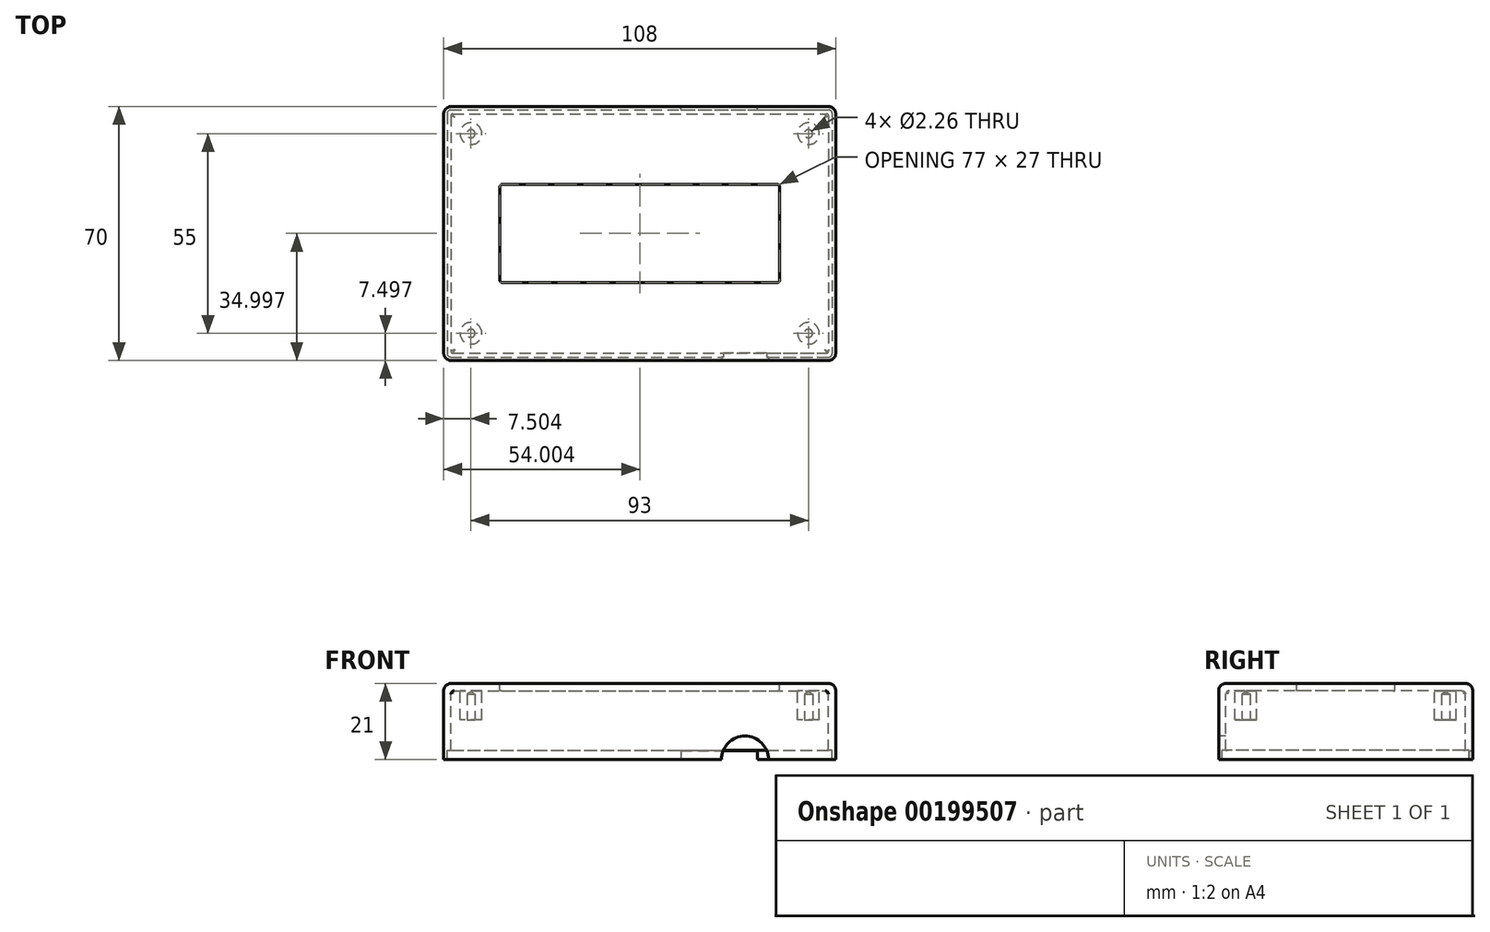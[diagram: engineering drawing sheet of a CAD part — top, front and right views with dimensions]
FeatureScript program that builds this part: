
annotation { "Feature Type Name" : "Feature", "Feature Type Description" : "" }
export const myFeature = defineFeature(function(context is Context, id is Id, definition is map)
    precondition{}
    {
        {
            var Q0;
            Q0=qCreatedBy(makeId("Top.planeOp"),FACE);
            var sketch = newSketch(context, id + "F0", { "sketchPlane" : qUnion([Q0])});
            skLineSegment(sketch, "E0.bottom", {"start": v(-55.54, 34.04) * mm, "end": v(48.46, 34.04) * mm});
            skLineSegment(sketch, "E0.top", {"start": v(-55.54, -35.96) * mm, "end": v(48.46, -35.96) * mm});
            skLineSegment(sketch, "E0.left", {"start": v(-57.54, 32.04) * mm, "end": v(-57.54, -33.96) * mm});
            skLineSegment(sketch, "E0.right", {"start": v(50.46, 32.04) * mm, "end": v(50.46, -33.96) * mm});
            skLineSegment(sketch, "E1.bottom", {"start": v(-41.54, 12.54) * mm, "end": v(34.46, 12.54) * mm});
            skLineSegment(sketch, "E1.top", {"start": v(-41.54, -14.46) * mm, "end": v(34.46, -14.46) * mm});
            skLineSegment(sketch, "E1.left", {"start": v(-42.04, 12.04) * mm, "end": v(-42.04, -13.96) * mm});
            skLineSegment(sketch, "E1.right", {"start": v(34.96, 12.04) * mm, "end": v(34.96, -13.96) * mm});
            skLineSegment(sketch, "E2.bottom", {"start": v(-55.04, 32.04) * mm, "end": v(47.96, 32.04) * mm});
            skLineSegment(sketch, "E2.top", {"start": v(-55.04, -33.96) * mm, "end": v(47.96, -33.96) * mm});
            skLineSegment(sketch, "E2.left", {"start": v(-55.54, 31.54) * mm, "end": v(-55.54, -33.46) * mm});
            skLineSegment(sketch, "E2.right", {"start": v(48.46, 31.54) * mm, "end": v(48.46, -33.46) * mm});
            skCircle(sketch, "E3", {"center": v(-50.04, 26.54) * mm, "radius": 3 * mm});
            skCircle(sketch, "E4", {"center": v(42.96, 26.54) * mm, "radius": 3 * mm});
            skCircle(sketch, "E5", {"center": v(-50.04, -28.46) * mm, "radius": 3 * mm});
            skCircle(sketch, "E6", {"center": v(42.96, -28.46) * mm, "radius": 3 * mm});
            skPoint(sketch, "E7.visualSharp", {"position": v(-55.54, -33.96) * mm});
            skPoint(sketch, "E8.visualSharp", {"position": v(-55.54, 32.04) * mm});
            skPoint(sketch, "E9.visualSharp", {"position": v(48.46, 32.04) * mm});
            skPoint(sketch, "E10.visualSharp", {"position": v(48.46, -33.96) * mm});
            skPoint(sketch, "E11.visualSharp", {"position": v(-57.54, 34.04) * mm});
            skPoint(sketch, "E12.visualSharp", {"position": v(50.46, 34.04) * mm});
            skPoint(sketch, "E13.visualSharp", {"position": v(50.46, -35.96) * mm});
            skLineSegment(sketch, "E14.bottom", {"start": v(-55.64, 33.09) * mm, "end": v(48.56, 33.09) * mm});
            skLineSegment(sketch, "E14.top", {"start": v(-55.64, -35.01) * mm, "end": v(48.56, -35.01) * mm});
            skLineSegment(sketch, "E14.left", {"start": v(-56.59, 32.14) * mm, "end": v(-56.59, -34.06) * mm});
            skLineSegment(sketch, "E14.right", {"start": v(49.51, 32.14) * mm, "end": v(49.51, -34.06) * mm});
            skPoint(sketch, "E15.visualSharp", {"position": v(-42.04, 12.54) * mm});
            skArc(sketch, "E15.filletArc", {"start": v(-41.54, 12.54) * mm, "mid": v(-41.89, 12.4) * mm, "end": v(-42.04, 12.04) * mm});
            skPoint(sketch, "E16.visualSharp", {"position": v(34.96, 12.54) * mm});
            skArc(sketch, "E16.filletArc", {"start": v(34.96, 12.04) * mm, "mid": v(34.82, 12.4) * mm, "end": v(34.46, 12.54) * mm});
            skPoint(sketch, "E17.visualSharp", {"position": v(34.96, -14.46) * mm});
            skArc(sketch, "E17.filletArc", {"start": v(34.46, -14.46) * mm, "mid": v(34.82, -14.32) * mm, "end": v(34.96, -13.96) * mm});
            skPoint(sketch, "E18.visualSharp", {"position": v(-42.04, -14.46) * mm});
            skArc(sketch, "E18.filletArc", {"start": v(-42.04, -13.96) * mm, "mid": v(-41.89, -14.32) * mm, "end": v(-41.54, -14.46) * mm});
            skArc(sketch, "E19.filletArc", {"start": v(-55.04, 32.04) * mm, "mid": v(-55.39, 31.9) * mm, "end": v(-55.54, 31.54) * mm});
            skArc(sketch, "E20.filletArc", {"start": v(48.46, 31.54) * mm, "mid": v(48.32, 31.9) * mm, "end": v(47.96, 32.04) * mm});
            skArc(sketch, "E21.filletArc", {"start": v(47.96, -33.96) * mm, "mid": v(48.32, -33.82) * mm, "end": v(48.46, -33.46) * mm});
            skArc(sketch, "E22.filletArc", {"start": v(-55.54, -33.46) * mm, "mid": v(-55.39, -33.82) * mm, "end": v(-55.04, -33.96) * mm});
            skPoint(sketch, "E23.visualSharp", {"position": v(-56.59, 33.09) * mm});
            skArc(sketch, "E23.filletArc", {"start": v(-55.64, 33.09) * mm, "mid": v(-56.3, 32.8) * mm, "end": v(-56.59, 32.14) * mm});
            skPoint(sketch, "E24.visualSharp", {"position": v(-56.59, -35.01) * mm});
            skArc(sketch, "E24.filletArc", {"start": v(-56.59, -34.06) * mm, "mid": v(-56.3, -34.73) * mm, "end": v(-55.64, -35.01) * mm});
            skPoint(sketch, "E25.visualSharp", {"position": v(49.51, -35.01) * mm});
            skArc(sketch, "E25.filletArc", {"start": v(48.56, -35.01) * mm, "mid": v(49.24, -34.73) * mm, "end": v(49.51, -34.06) * mm});
            skPoint(sketch, "E26.visualSharp", {"position": v(49.51, 33.09) * mm});
            skArc(sketch, "E26.filletArc", {"start": v(49.51, 32.14) * mm, "mid": v(49.24, 32.8) * mm, "end": v(48.56, 33.09) * mm});
            skArc(sketch, "E27.filletArc", {"start": v(50.46, 32.04) * mm, "mid": v(49.88, 33.45) * mm, "end": v(48.46, 34.04) * mm});
            skArc(sketch, "E28.filletArc", {"start": v(48.46, -35.96) * mm, "mid": v(49.88, -35.38) * mm, "end": v(50.46, -33.96) * mm});
            skPoint(sketch, "E29.visualSharp", {"position": v(-57.54, -35.96) * mm});
            skArc(sketch, "E29.filletArc", {"start": v(-57.54, -33.96) * mm, "mid": v(-56.95, -35.38) * mm, "end": v(-55.54, -35.96) * mm});
            skArc(sketch, "E30.filletArc", {"start": v(-55.54, 34.04) * mm, "mid": v(-56.95, 33.45) * mm, "end": v(-57.54, 32.04) * mm});
            skSolve(sketch);
        }
        {
            var Q0;
            Q0=makeQuery(id+"F0.imprint","IMPRINT",FACE,{"disambiguationData":[TD([[makeQuery(id+"F0.imprint","IMPRINT",EDGE,{"derivedFrom":sQuery(id+"F0.wireOp",EDGE,"E2.bottom")}),1.0]])]});
            var Q1;
            Q1=makeQuery(id+"F0.imprint","IMPRINT",FACE,{"disambiguationData":[TD([[makeQuery(id+"F0.imprint","IMPRINT",EDGE,{"derivedFrom":sQuery(id+"F0.wireOp",EDGE,"E2.bottom")}),-1.0]])]});
            var Q2;
            Q2=makeQuery(id+"F0.imprint","IMPRINT",FACE,{"disambiguationData":[TD([[makeQuery(id+"F0.imprint","IMPRINT",EDGE,{"derivedFrom":sQuery(id+"F0.wireOp",EDGE,"E3")}),1.0]])]});
            var Q3;
            Q3=makeQuery(id+"F0.imprint","IMPRINT",FACE,{"disambiguationData":[TD([[makeQuery(id+"F0.imprint","IMPRINT",EDGE,{"derivedFrom":sQuery(id+"F0.wireOp",EDGE,"E4")}),1.0]])]});
            var Q4;
            Q4=makeQuery(id+"F0.imprint","IMPRINT",FACE,{"disambiguationData":[TD([[makeQuery(id+"F0.imprint","IMPRINT",EDGE,{"derivedFrom":sQuery(id+"F0.wireOp",EDGE,"E6")}),1.0]])]});
            var Q5;
            Q5=makeQuery(id+"F0.imprint","IMPRINT",FACE,{"disambiguationData":[TD([[makeQuery(id+"F0.imprint","IMPRINT",EDGE,{"derivedFrom":sQuery(id+"F0.wireOp",EDGE,"E5")}),1.0]])]});
            var Q6;
            Q6=makeQuery(id+"F0.imprint","IMPRINT",FACE,{"disambiguationData":[TD([[makeQuery(id+"F0.imprint","IMPRINT",EDGE,{"derivedFrom":sQuery(id+"F0.wireOp",EDGE,"E0.bottom")}),-1.0]])]});
            extrude(context, id + "F1", {"entities" : qUnion([Q0, Q1, Q2, Q3, Q4, Q5, Q6]), "oppositeDirection" : true, "depth" : 2 * mm});
        }
        {
            var Q0;
            Q0=makeQuery(id+"F0.imprint","IMPRINT",FACE,{"disambiguationData":[TD([[makeQuery(id+"F0.imprint","IMPRINT",EDGE,{"derivedFrom":sQuery(id+"F0.wireOp",EDGE,"E2.bottom")}),1.0]])]});
            extrude(context, id + "F2", {"entities" : qUnion([Q0]), "operationType" : NewBodyOperationType.ADD, "oppositeDirection" : true, "depth" : 18.49 * mm});
        }
        {
            var Q0;
            {var subQ0=sQuery(id+"F0.wireOp",EDGE,"E0.right");var subQ1=sQuery(id+"F0.wireOp",EDGE,"E0.left");var subQ2=sQuery(id+"F0.wireOp",EDGE,"E0.top");var subQ3=sQuery(id+"F0.wireOp",EDGE,"E0.bottom");Q0=makeQuery(id+"F2.boolean.opBoolean","SPLIT",FACE,{"disambiguationData":[TD([makeQuery(id+"F1.opExtrude","SWEPT_FACE",FACE,{"disambiguationData":[OSD([subQ3])]})])],"derivedFrom":makeQuery(id+"F1.opExtrude","CAP_FACE",FACE,{"disambiguationData":[OSD([subQ3,subQ2,subQ1,subQ0,sQuery(id+"F0.wireOp",EDGE,"E1.bottom"),sQuery(id+"F0.wireOp",EDGE,"E1.top"),sQuery(id+"F0.wireOp",EDGE,"E1.left"),sQuery(id+"F0.wireOp",EDGE,"E1.right"),sQuery(id+"F0.wireOp",EDGE,"TIqVLyNP-uRYi-IZCg-FFMY-wpAB1gUjtPzc"),sQuery(id+"F0.wireOp",EDGE,"eGpXYtko-bpSR-Pbzy-FSSL-hkfkqHyOyQKH"),sQuery(id+"F0.wireOp",EDGE,"aKAKSCUs-jV2O-gDTW-lYoO-wS98vJuitCCh"),sQuery(id+"F0.wireOp",EDGE,"Y9MBlFMN-f0e3-QmNQ-qzjT-em0skZvg3ODU")])],"isStart":false})});}
            extrude(context, id + "F3", {"entities" : qUnion([Q0]), "operationType" : NewBodyOperationType.ADD, "depth" : 19 * mm});
        }
        {
            var Q0;
            Q0=makeQuery(id+"F0.imprint","IMPRINT",FACE,{"disambiguationData":[TD([[makeQuery(id+"F0.imprint","IMPRINT",EDGE,{"derivedFrom":sQuery(id+"F0.wireOp",EDGE,"E3")}),1.0]])]});
            var Q1;
            Q1=makeQuery(id+"F0.imprint","IMPRINT",FACE,{"disambiguationData":[TD([[makeQuery(id+"F0.imprint","IMPRINT",EDGE,{"derivedFrom":sQuery(id+"F0.wireOp",EDGE,"E4")}),1.0]])]});
            var Q2;
            Q2=makeQuery(id+"F0.imprint","IMPRINT",FACE,{"disambiguationData":[TD([[makeQuery(id+"F0.imprint","IMPRINT",EDGE,{"derivedFrom":sQuery(id+"F0.wireOp",EDGE,"E5")}),1.0]])]});
            var Q3;
            Q3=makeQuery(id+"F0.imprint","IMPRINT",FACE,{"disambiguationData":[TD([[makeQuery(id+"F0.imprint","IMPRINT",EDGE,{"derivedFrom":sQuery(id+"F0.wireOp",EDGE,"E6")}),1.0]])]});
            extrude(context, id + "F4", {"entities" : qUnion([Q0, Q1, Q2, Q3]), "operationType" : NewBodyOperationType.ADD, "oppositeDirection" : true, "depth" : 10 * mm});
        }
        {
            var Q0;
            {var subQ0=sQuery(id+"F0.wireOp",EDGE,"E0.top");Q0=makeQuery(id+"F3.boolean.opBoolean","MERGE",FACE,{"derivedFrom":[makeQuery(id+"F1.opExtrude","SWEPT_FACE",FACE,{"disambiguationData":[OSD([subQ0])]}),makeQuery(id+"F3.opExtrude","SWEPT_FACE",FACE,{"disambiguationData":[OSD([subQ0])]})]});}
            var sketch = newSketch(context, id + "F5", { "sketchPlane" : qUnion([Q0])});
            skPoint(sketch, "E31", {"position": v(25.46, -21) * mm});
            skCircle(sketch, "E32", {"center": v(25.46, -21) * mm, "radius": 6.5 * mm});
            skSolve(sketch);
        }
        {
            var Q0;
            {var subQ0=sQuery(id+"F5.wireOp",EDGE,"E32");var subQ1=makeQuery(id+"F3.opExtrude","CAP_EDGE",EDGE,{"disambiguationData":[OSD([sQuery(id+"F0.wireOp",EDGE,"E0.top")])],"isStart":false});var subQ2=makeQuery(id+"F5.imprint","INTERSECT",VERTEX,{"disambiguationData":[OD(0.0)],"derivedFrom":[subQ1,subQ0]});Q0=makeQuery(id+"F5.imprint","IMPRINT",FACE,{"disambiguationData":[TD([[makeQuery(id+"F5.imprint","IMPRINT",EDGE,{"disambiguationData":[TD([[subQ2,1.0]])],"derivedFrom":subQ0}),1.0]])]});}
            extrude(context, id + "F6", {"entities" : qUnion([Q0]), "operationType" : NewBodyOperationType.REMOVE, "oppositeDirection" : true, "depth" : 2.5 * mm});
        }
        {
            var Q0;
            {var subQ0=sQuery(id+"F0.wireOp",EDGE,"E0.bottom");Q0=makeQuery(id+"F3.boolean.opBoolean","MERGE",FACE,{"derivedFrom":[makeQuery(id+"F1.opExtrude","SWEPT_FACE",FACE,{"disambiguationData":[OSD([subQ0])]}),makeQuery(id+"F3.opExtrude","SWEPT_FACE",FACE,{"disambiguationData":[OSD([subQ0])]})]});}
            var sketch = newSketch(context, id + "F7", { "sketchPlane" : qUnion([Q0])});
            skLineSegment(sketch, "E33.bottom", {"start": v(-28.86, -21) * mm, "end": v(-7.86, -21) * mm});
            skLineSegment(sketch, "E33.top", {"start": v(-28.86, -18.6) * mm, "end": v(-7.86, -18.6) * mm});
            skLineSegment(sketch, "E33.left", {"start": v(-28.86, -21) * mm, "end": v(-28.86, -18.6) * mm});
            skLineSegment(sketch, "E33.right", {"start": v(-7.86, -21) * mm, "end": v(-7.86, -18.6) * mm});
            skSolve(sketch);
        }
        {
            var Q0;
            Q0=makeQuery(id+"F7.imprint","IMPRINT",FACE,{"disambiguationData":[TD([[makeQuery(id+"F7.imprint","IMPRINT",EDGE,{"derivedFrom":sQuery(id+"F7.wireOp",EDGE,"E33.bottom")}),-1.0]])]});
            extrude(context, id + "F8", {"entities" : qUnion([Q0]), "operationType" : NewBodyOperationType.REMOVE, "oppositeDirection" : true, "depth" : 2.5 * mm});
        }
        {
            var Q0;
            Q0=makeQuery(id+"F4.opExtrude","CAP_FACE",FACE,{"disambiguationData":[OSD([sQuery(id+"F0.wireOp",EDGE,"E6")])],"isStart":false});
            var sketch = newSketch(context, id + "F9", { "sketchPlane" : qUnion([Q0])});
            skPoint(sketch, "E34", {"position": v(-50.04, -26.54) * mm});
            skPoint(sketch, "E35", {"position": v(42.96, -26.54) * mm});
            skPoint(sketch, "E36", {"position": v(42.96, 28.46) * mm});
            skPoint(sketch, "E37", {"position": v(-50.04, 28.46) * mm});
            skSolve(sketch);
        }
        {
            var Q0;
            Q0=sQuery(id+"F9.wireOp",VERTEX,"E34");
            var Q1;
            Q1=sQuery(id+"F9.wireOp",VERTEX,"E35");
            var Q2;
            Q2=sQuery(id+"F9.wireOp",VERTEX,"E36");
            var Q3;
            Q3=sQuery(id+"F9.wireOp",VERTEX,"E37");
            var Q4;
            Q4=makeQuery(id+"F1.opExtrude","SWEPT_BODY",BODY,{"disambiguationData":[OSD([sQuery(id+"F0.wireOp",EDGE,"E0.bottom"),sQuery(id+"F0.wireOp",EDGE,"E0.top"),sQuery(id+"F0.wireOp",EDGE,"E0.left"),sQuery(id+"F0.wireOp",EDGE,"E0.right"),sQuery(id+"F0.wireOp",EDGE,"E1.bottom"),sQuery(id+"F0.wireOp",EDGE,"E1.top"),sQuery(id+"F0.wireOp",EDGE,"E1.left"),sQuery(id+"F0.wireOp",EDGE,"E1.right"),sQuery(id+"F0.wireOp",EDGE,"TIqVLyNP-uRYi-IZCg-FFMY-wpAB1gUjtPzc"),sQuery(id+"F0.wireOp",EDGE,"eGpXYtko-bpSR-Pbzy-FSSL-hkfkqHyOyQKH"),sQuery(id+"F0.wireOp",EDGE,"aKAKSCUs-jV2O-gDTW-lYoO-wS98vJuitCCh"),sQuery(id+"F0.wireOp",EDGE,"Y9MBlFMN-f0e3-QmNQ-qzjT-em0skZvg3ODU")])]});
            hole(context, id + "F10", {"style" : HoleStyle.SIMPLE, "endStyle" : HoleEndStyle.BLIND, "standardTappedOrClearance" : lookupTablePath({ "standard" : "ANSI", "size" : "#43 (0.09)", "type" : "Drilled" }), "standardBlindInLast" : lookupTablePath({ "standard" : "ANSI", "size" : "#43", "type" : "Drilled" }), "holeDiameter" : 2.26 * mm, "holeDepth" : 7 * mm, "tappedDepth" : 12 * mm, "tapClearance" : 3, "startFromSketch" : true, "locations" : qUnion([Q0, Q1, Q2, Q3]), "scope" : qUnion([Q4])});
        }
        {
            var Q0;
            Q0=makeQuery(id+"F1.opExtrude","CAP_EDGE",EDGE,{"disambiguationData":[OSD([sQuery(id+"F0.wireOp",EDGE,"E0.left")])],"isStart":true});
            var Q1;
            Q1=makeQuery(id+"F1.opExtrude","CAP_EDGE",EDGE,{"disambiguationData":[OSD([sQuery(id+"F0.wireOp",EDGE,"E0.bottom")])],"isStart":true});
            var Q2;
            Q2=makeQuery(id+"F1.opExtrude","CAP_EDGE",EDGE,{"disambiguationData":[OSD([sQuery(id+"F0.wireOp",EDGE,"E0.right")])],"isStart":true});
            var Q3;
            {var subQ0=sQuery(id+"F0.wireOp",EDGE,"E0.right");var subQ1=sQuery(id+"F0.wireOp",EDGE,"E0.top");Q3=makeQuery(id+"F3.boolean.opBoolean","MERGE",EDGE,{"derivedFrom":[makeQuery(id+"F1.opExtrude","SWEPT_EDGE",EDGE,{"disambiguationData":[OSD([subQ1,subQ0])]}),makeQuery(id+"F3.opExtrude","SWEPT_EDGE",EDGE,{"disambiguationData":[OSD([subQ1,subQ0])]})]});}
            var Q4;
            Q4=makeQuery(id+"F1.opExtrude","CAP_EDGE",EDGE,{"disambiguationData":[OSD([sQuery(id+"F0.wireOp",EDGE,"E0.top")])],"isStart":true});
            var Q5;
            {var subQ0=sQuery(id+"F0.wireOp",EDGE,"E0.left");var subQ1=sQuery(id+"F0.wireOp",EDGE,"E0.top");Q5=makeQuery(id+"F3.boolean.opBoolean","MERGE",EDGE,{"derivedFrom":[makeQuery(id+"F1.opExtrude","SWEPT_EDGE",EDGE,{"disambiguationData":[OSD([subQ1,subQ0])]}),makeQuery(id+"F3.opExtrude","SWEPT_EDGE",EDGE,{"disambiguationData":[OSD([subQ1,subQ0])]})]});}
            var Q6;
            {var subQ0=sQuery(id+"F0.wireOp",EDGE,"E0.right");var subQ1=sQuery(id+"F0.wireOp",EDGE,"E0.bottom");Q6=makeQuery(id+"F3.boolean.opBoolean","MERGE",EDGE,{"derivedFrom":[makeQuery(id+"F1.opExtrude","SWEPT_EDGE",EDGE,{"disambiguationData":[OSD([subQ1,subQ0])]}),makeQuery(id+"F3.opExtrude","SWEPT_EDGE",EDGE,{"disambiguationData":[OSD([subQ1,subQ0])]})]});}
            var Q7;
            {var subQ0=sQuery(id+"F0.wireOp",EDGE,"E0.left");var subQ1=sQuery(id+"F0.wireOp",EDGE,"E0.bottom");Q7=makeQuery(id+"F3.boolean.opBoolean","MERGE",EDGE,{"derivedFrom":[makeQuery(id+"F1.opExtrude","SWEPT_EDGE",EDGE,{"disambiguationData":[OSD([subQ1,subQ0])]}),makeQuery(id+"F3.opExtrude","SWEPT_EDGE",EDGE,{"disambiguationData":[OSD([subQ1,subQ0])]})]});}
            fillet(context, id + "F11", {"entities" : qUnion([Q0, Q1, Q2, Q3, Q4, Q5, Q6, Q7]), "radius" : 2 * mm, "tangentPropagation" : true, "allowEdgeOverflow" : false});
        }
        {
            var Q0;
            Q0=makeQuery(id+"F2.opExtrude","SWEPT_EDGE",EDGE,{"disambiguationData":[OSD([sQuery(id+"F0.wireOp",EDGE,"E2.top"),sQuery(id+"F0.wireOp",EDGE,"E2.right")])]});
            var Q1;
            Q1=makeQuery(id+"F2.boolean.opBoolean","INTERSECT",EDGE,{"derivedFrom":[makeQuery(id+"F1.opExtrude","CAP_FACE",FACE,{"disambiguationData":[OSD([sQuery(id+"F0.wireOp",EDGE,"E0.bottom"),sQuery(id+"F0.wireOp",EDGE,"E0.top"),sQuery(id+"F0.wireOp",EDGE,"E0.left"),sQuery(id+"F0.wireOp",EDGE,"E0.right"),sQuery(id+"F0.wireOp",EDGE,"E1.bottom"),sQuery(id+"F0.wireOp",EDGE,"E1.top"),sQuery(id+"F0.wireOp",EDGE,"E1.left"),sQuery(id+"F0.wireOp",EDGE,"E1.right"),sQuery(id+"F0.wireOp",EDGE,"TIqVLyNP-uRYi-IZCg-FFMY-wpAB1gUjtPzc"),sQuery(id+"F0.wireOp",EDGE,"eGpXYtko-bpSR-Pbzy-FSSL-hkfkqHyOyQKH"),sQuery(id+"F0.wireOp",EDGE,"aKAKSCUs-jV2O-gDTW-lYoO-wS98vJuitCCh"),sQuery(id+"F0.wireOp",EDGE,"Y9MBlFMN-f0e3-QmNQ-qzjT-em0skZvg3ODU")])],"isStart":false}),makeQuery(id+"F2.opExtrude","SWEPT_FACE",FACE,{"disambiguationData":[OSD([sQuery(id+"F0.wireOp",EDGE,"E2.right")])]})]});
            var Q2;
            Q2=makeQuery(id+"F2.boolean.opBoolean","INTERSECT",EDGE,{"derivedFrom":[makeQuery(id+"F1.opExtrude","CAP_FACE",FACE,{"disambiguationData":[OSD([sQuery(id+"F0.wireOp",EDGE,"E0.bottom"),sQuery(id+"F0.wireOp",EDGE,"E0.top"),sQuery(id+"F0.wireOp",EDGE,"E0.left"),sQuery(id+"F0.wireOp",EDGE,"E0.right"),sQuery(id+"F0.wireOp",EDGE,"E1.bottom"),sQuery(id+"F0.wireOp",EDGE,"E1.top"),sQuery(id+"F0.wireOp",EDGE,"E1.left"),sQuery(id+"F0.wireOp",EDGE,"E1.right"),sQuery(id+"F0.wireOp",EDGE,"TIqVLyNP-uRYi-IZCg-FFMY-wpAB1gUjtPzc"),sQuery(id+"F0.wireOp",EDGE,"eGpXYtko-bpSR-Pbzy-FSSL-hkfkqHyOyQKH"),sQuery(id+"F0.wireOp",EDGE,"aKAKSCUs-jV2O-gDTW-lYoO-wS98vJuitCCh"),sQuery(id+"F0.wireOp",EDGE,"Y9MBlFMN-f0e3-QmNQ-qzjT-em0skZvg3ODU")])],"isStart":false}),makeQuery(id+"F2.opExtrude","SWEPT_FACE",FACE,{"disambiguationData":[OSD([sQuery(id+"F0.wireOp",EDGE,"E2.top")])]})]});
            var Q3;
            Q3=makeQuery(id+"F2.opExtrude","SWEPT_EDGE",EDGE,{"disambiguationData":[OSD([sQuery(id+"F0.wireOp",EDGE,"E2.top"),sQuery(id+"F0.wireOp",EDGE,"E2.left")])]});
            var Q4;
            Q4=makeQuery(id+"F2.boolean.opBoolean","INTERSECT",EDGE,{"derivedFrom":[makeQuery(id+"F1.opExtrude","CAP_FACE",FACE,{"disambiguationData":[OSD([sQuery(id+"F0.wireOp",EDGE,"E0.bottom"),sQuery(id+"F0.wireOp",EDGE,"E0.top"),sQuery(id+"F0.wireOp",EDGE,"E0.left"),sQuery(id+"F0.wireOp",EDGE,"E0.right"),sQuery(id+"F0.wireOp",EDGE,"E1.bottom"),sQuery(id+"F0.wireOp",EDGE,"E1.top"),sQuery(id+"F0.wireOp",EDGE,"E1.left"),sQuery(id+"F0.wireOp",EDGE,"E1.right"),sQuery(id+"F0.wireOp",EDGE,"TIqVLyNP-uRYi-IZCg-FFMY-wpAB1gUjtPzc"),sQuery(id+"F0.wireOp",EDGE,"eGpXYtko-bpSR-Pbzy-FSSL-hkfkqHyOyQKH"),sQuery(id+"F0.wireOp",EDGE,"aKAKSCUs-jV2O-gDTW-lYoO-wS98vJuitCCh"),sQuery(id+"F0.wireOp",EDGE,"Y9MBlFMN-f0e3-QmNQ-qzjT-em0skZvg3ODU")])],"isStart":false}),makeQuery(id+"F2.opExtrude","SWEPT_FACE",FACE,{"disambiguationData":[OSD([sQuery(id+"F0.wireOp",EDGE,"E2.left")])]})]});
            var Q5;
            Q5=makeQuery(id+"F2.opExtrude","SWEPT_EDGE",EDGE,{"disambiguationData":[OSD([sQuery(id+"F0.wireOp",EDGE,"E2.bottom"),sQuery(id+"F0.wireOp",EDGE,"E2.left")])]});
            var Q6;
            Q6=makeQuery(id+"F2.boolean.opBoolean","INTERSECT",EDGE,{"derivedFrom":[makeQuery(id+"F1.opExtrude","CAP_FACE",FACE,{"disambiguationData":[OSD([sQuery(id+"F0.wireOp",EDGE,"E0.bottom"),sQuery(id+"F0.wireOp",EDGE,"E0.top"),sQuery(id+"F0.wireOp",EDGE,"E0.left"),sQuery(id+"F0.wireOp",EDGE,"E0.right"),sQuery(id+"F0.wireOp",EDGE,"E1.bottom"),sQuery(id+"F0.wireOp",EDGE,"E1.top"),sQuery(id+"F0.wireOp",EDGE,"E1.left"),sQuery(id+"F0.wireOp",EDGE,"E1.right"),sQuery(id+"F0.wireOp",EDGE,"TIqVLyNP-uRYi-IZCg-FFMY-wpAB1gUjtPzc"),sQuery(id+"F0.wireOp",EDGE,"eGpXYtko-bpSR-Pbzy-FSSL-hkfkqHyOyQKH"),sQuery(id+"F0.wireOp",EDGE,"aKAKSCUs-jV2O-gDTW-lYoO-wS98vJuitCCh"),sQuery(id+"F0.wireOp",EDGE,"Y9MBlFMN-f0e3-QmNQ-qzjT-em0skZvg3ODU")])],"isStart":false}),makeQuery(id+"F2.opExtrude","SWEPT_FACE",FACE,{"disambiguationData":[OSD([sQuery(id+"F0.wireOp",EDGE,"E2.bottom")])]})]});
            var Q7;
            Q7=makeQuery(id+"F2.opExtrude","SWEPT_EDGE",EDGE,{"disambiguationData":[OSD([sQuery(id+"F0.wireOp",EDGE,"E2.bottom"),sQuery(id+"F0.wireOp",EDGE,"E2.right")])]});
            fillet(context, id + "F12", {"entities" : qUnion([Q0, Q1, Q2, Q3, Q4, Q5, Q6, Q7]), "radius" : 1 * mm, "tangentPropagation" : true, "allowEdgeOverflow" : false});
        }
    });
